# Revit family: OASIS SH3P-3937
name_source: partatom
category: Plumbing Fixtures
units: mm (PartAtom-declared; Revit-internal decimal feet)

## family parameters
Always vertical = Yes
Cut with Voids When Loaded = No
OmniClass Number = 23.45.05.14.21.11
OmniClass Title = Bath/Shower Units
Part Type = Normal
Room Calculation Point = No
Round Connector Dimension = Use Diameter
Shared = No
Work Plane-Based = No

## types (5) — shared parameters
BIM Model By = www.epoch-design.com
Cold Water Connector = Cold Water Connection
Color = <By Category>
Default Elevation = 0"
Grab Bar Finish = <By Category>
Hot Water Connector = Hot Water Connection
Manufacturer = OASIS
Model = SH3P-MD-6032/(3SF, 3SM, FH, TLRF)
Sanitary Connector = Sanitary Connection
Seat Finish = <By Category>
Stainless steel = <By Category>
Type Comments = SHOWER
URL = www.oasisbath.com
Waste Connection = No

## per-type parameters (varying)
| type | Bar_Horz_Corner | Bar_Vert | NO_Bar_Vert | Seat_Fold | Shower Rod |
| Base Model, 3SF, 3SM, FH, & FHV packages | No | No | Yes | No | No |
| 2BAR package | Yes | Yes | No | No | No |
| ICBAR package | Yes | No | Yes | No | No |
| ADA-10 package | Yes | No | Yes | Yes | Yes |
| ANS17 package | Yes | Yes | No | Yes | Yes |

## geometry (parser evidence)
native form markers: Sweep x14
no freeform markers — native parametric forms only
